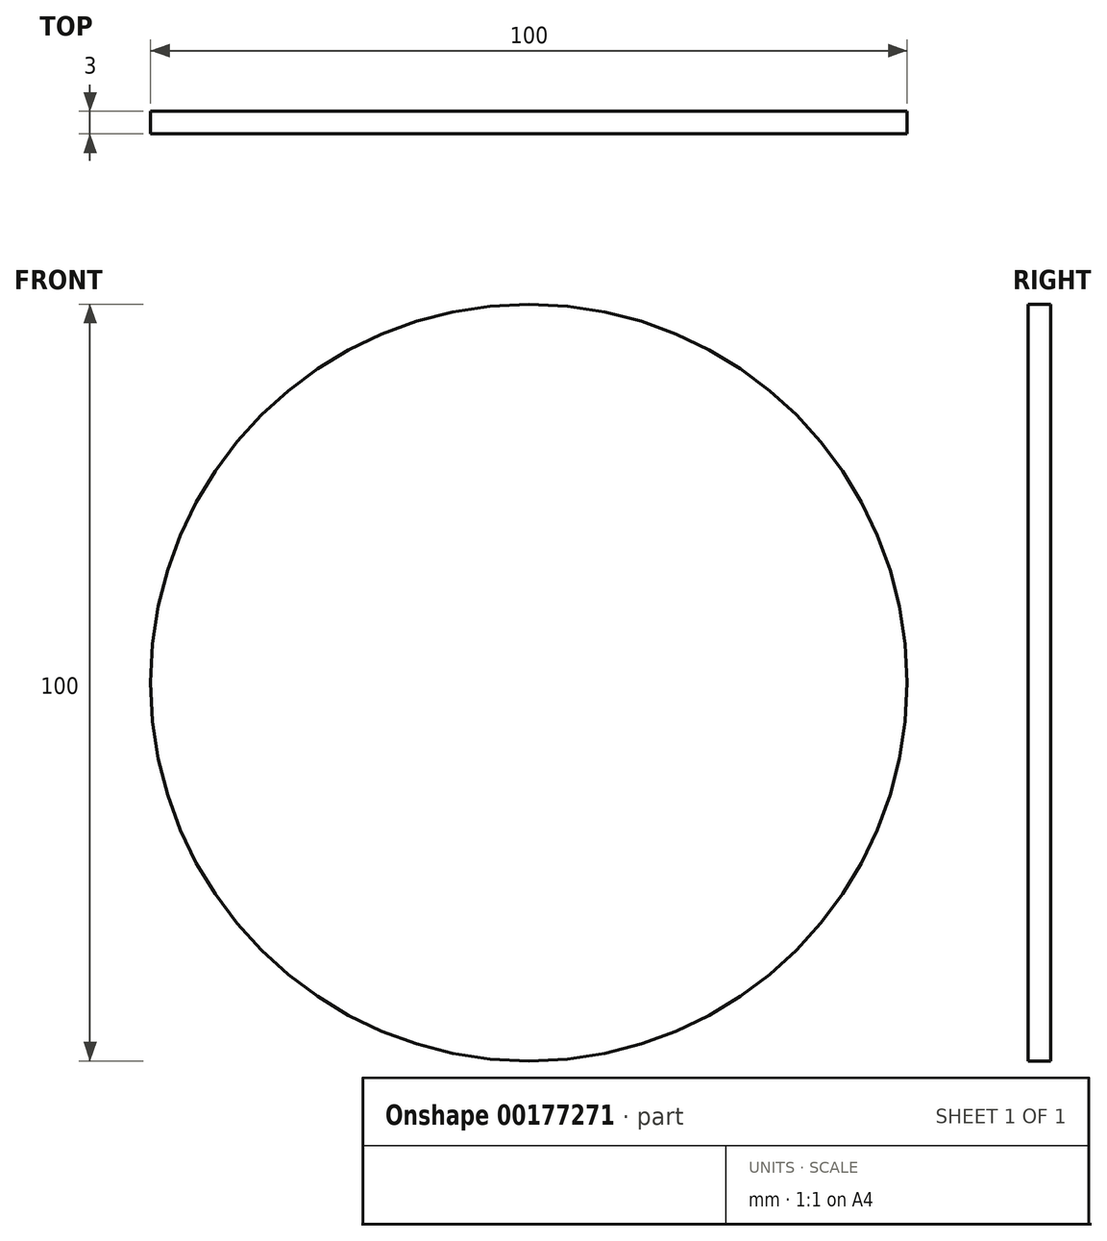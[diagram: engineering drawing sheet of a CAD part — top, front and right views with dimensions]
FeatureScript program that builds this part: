
annotation { "Feature Type Name" : "Feature", "Feature Type Description" : "" }
export const myFeature = defineFeature(function(context is Context, id is Id, definition is map)
    precondition{}
    {
        {
            var Q0;
            Q0=qCreatedBy(makeId("Front.planeOp"),FACE);
            var sketch = newSketch(context, id + "F0", { "sketchPlane" : qUnion([Q0])});
            skCircle(sketch, "E0", {"center": v(0, 0) * mm, "radius": 50 * mm});
            skSolve(sketch);
        }
        {
            var Q0;
            Q0 = qSketchRegion(id + "F0", true);
            extrude(context, id + "F1", {"entities" : qUnion([Q0]), "depth" : 3 * mm});
        }
    });
